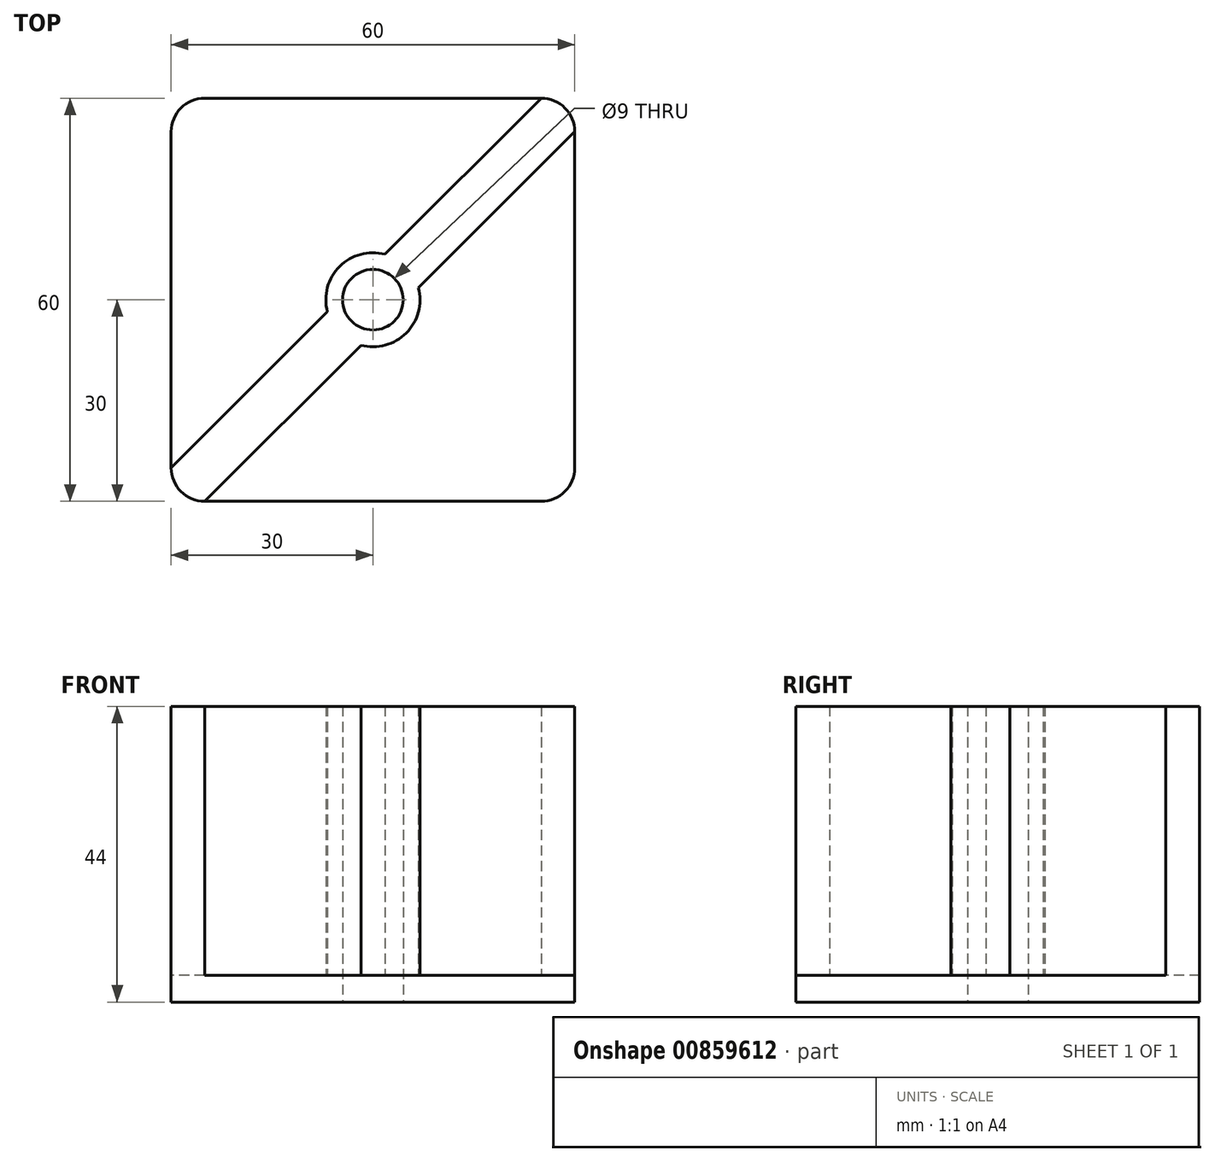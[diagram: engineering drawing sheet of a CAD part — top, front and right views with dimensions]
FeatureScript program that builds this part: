
annotation { "Feature Type Name" : "Feature", "Feature Type Description" : "" }
export const myFeature = defineFeature(function(context is Context, id is Id, definition is map)
    precondition{}
    {
        {
            var Q0;
            Q0=qCreatedBy(makeId("Top.planeOp"),FACE);
            var sketch = newSketch(context, id + "F0", { "sketchPlane" : qUnion([Q0])});
            skLineSegment(sketch, "E0.bottom", {"start": v(25, -30) * mm, "end": v(-25, -30) * mm});
            skLineSegment(sketch, "E0.top", {"start": v(25, 30) * mm, "end": v(-25, 30) * mm});
            skLineSegment(sketch, "E0.left", {"start": v(30, -25) * mm, "end": v(30, 25) * mm});
            skLineSegment(sketch, "E0.right", {"start": v(-30, -25) * mm, "end": v(-30, 25) * mm});
            skPoint(sketch, "E0.middle", {"position": v(0, 0) * mm});
            skPoint(sketch, "E1.visualSharp", {"position": v(-30, 30) * mm});
            skArc(sketch, "E1.filletArc", {"start": v(-25, 30) * mm, "mid": v(-28.54, 28.54) * mm, "end": v(-30, 25) * mm});
            skPoint(sketch, "E2.visualSharp", {"position": v(30, 30) * mm});
            skArc(sketch, "E2.filletArc", {"start": v(30, 25) * mm, "mid": v(28.54, 28.54) * mm, "end": v(25, 30) * mm});
            skPoint(sketch, "E3.visualSharp", {"position": v(30, -30) * mm});
            skArc(sketch, "E3.filletArc", {"start": v(25, -30) * mm, "mid": v(28.54, -28.54) * mm, "end": v(30, -25) * mm});
            skPoint(sketch, "E4.visualSharp", {"position": v(-30, -30) * mm});
            skArc(sketch, "E4.filletArc", {"start": v(-30, -25) * mm, "mid": v(-28.54, -28.54) * mm, "end": v(-25, -30) * mm});
            skSolve(sketch);
        }
        {
            var Q0;
            Q0=makeQuery(id+"F0.imprint","IMPRINT",FACE,{"disambiguationData":[TD([[makeQuery(id+"F0.imprint","IMPRINT",EDGE,{"derivedFrom":sQuery(id+"F0.wireOp",EDGE,"E0.top")}),1.0]])]});
            var Q1;
            Q1=makeQuery(id+"F0.imprint","IMPRINT",FACE,{"disambiguationData":[TD([[makeQuery(id+"F0.imprint","IMPRINT",EDGE,{"derivedFrom":sQuery(id+"F0.wireOp",EDGE,"E0.bottom")}),-1.0]])]});
            extrude(context, id + "F1", {"entities" : qUnion([Q0, Q1]), "depth" : 4 * mm, "offsetDistance" : 25 * mm});
        }
        {
            var Q0;
            Q0=makeQuery(id+"F1.opExtrude","CAP_FACE",FACE,{"disambiguationData":[OSD([sQuery(id+"F0.wireOp",EDGE,"E0.bottom"),sQuery(id+"F0.wireOp",EDGE,"E0.top"),sQuery(id+"F0.wireOp",EDGE,"E0.left"),sQuery(id+"F0.wireOp",EDGE,"E0.right"),sQuery(id+"F0.wireOp",EDGE,"E1.filletArc"),sQuery(id+"F0.wireOp",EDGE,"E2.filletArc"),sQuery(id+"F0.wireOp",EDGE,"E3.filletArc"),sQuery(id+"F0.wireOp",EDGE,"E4.filletArc")])],"isStart":false});
            var sketch = newSketch(context, id + "F2", { "sketchPlane" : qUnion([Q0])});
            skCircle(sketch, "E5", {"center": v(0, 0) * mm, "radius": 4.5 * mm});
            skArc(sketch, "E6", {"start": v(1.77, 6.77) * mm, "mid": v(-4.95, 4.95) * mm, "end": v(-6.77, -1.77) * mm});
            skLineSegment(sketch, "E7", {"start": v(25, 30) * mm, "end": v(1.77, 6.77) * mm});
            skLineSegment(sketch, "E8", {"start": v(-25, -30) * mm, "end": v(-1.77, -6.77) * mm});
            skLineSegment(sketch, "E9.trimOffspring", {"start": v(-6.77, -1.77) * mm, "end": v(-30, -25) * mm});
            skLineSegment(sketch, "E10.trimOffspring", {"start": v(6.77, 1.77) * mm, "end": v(30, 25) * mm});
            skArc(sketch, "E11.trimOffspring", {"start": v(-1.77, -6.77) * mm, "mid": v(4.95, -4.95) * mm, "end": v(6.77, 1.77) * mm});
            skSolve(sketch);
        }
        {
            var Q0;
            Q0=makeQuery(id+"F2.imprint","IMPRINT",FACE,{"disambiguationData":[TD([[makeQuery(id+"F2.imprint","IMPRINT",EDGE,{"derivedFrom":sQuery(id+"F2.wireOp",EDGE,"E5")}),-1.0]])]});
            extrude(context, id + "F3", {"entities" : qUnion([Q0]), "operationType" : NewBodyOperationType.ADD, "depth" : 40 * mm, "offsetDistance" : 25 * mm});
        }
        {
            var Q0;
            Q0=makeQuery(id+"F2.imprint","IMPRINT",FACE,{"disambiguationData":[TD([[makeQuery(id+"F2.imprint","IMPRINT",EDGE,{"derivedFrom":sQuery(id+"F2.wireOp",EDGE,"E5")}),1.0]])]});
            extrude(context, id + "F4", {"entities" : qUnion([Q0]), "operationType" : NewBodyOperationType.REMOVE, "oppositeDirection" : true, "depth" : 25 * mm, "offsetDistance" : 25 * mm});
        }
    });
